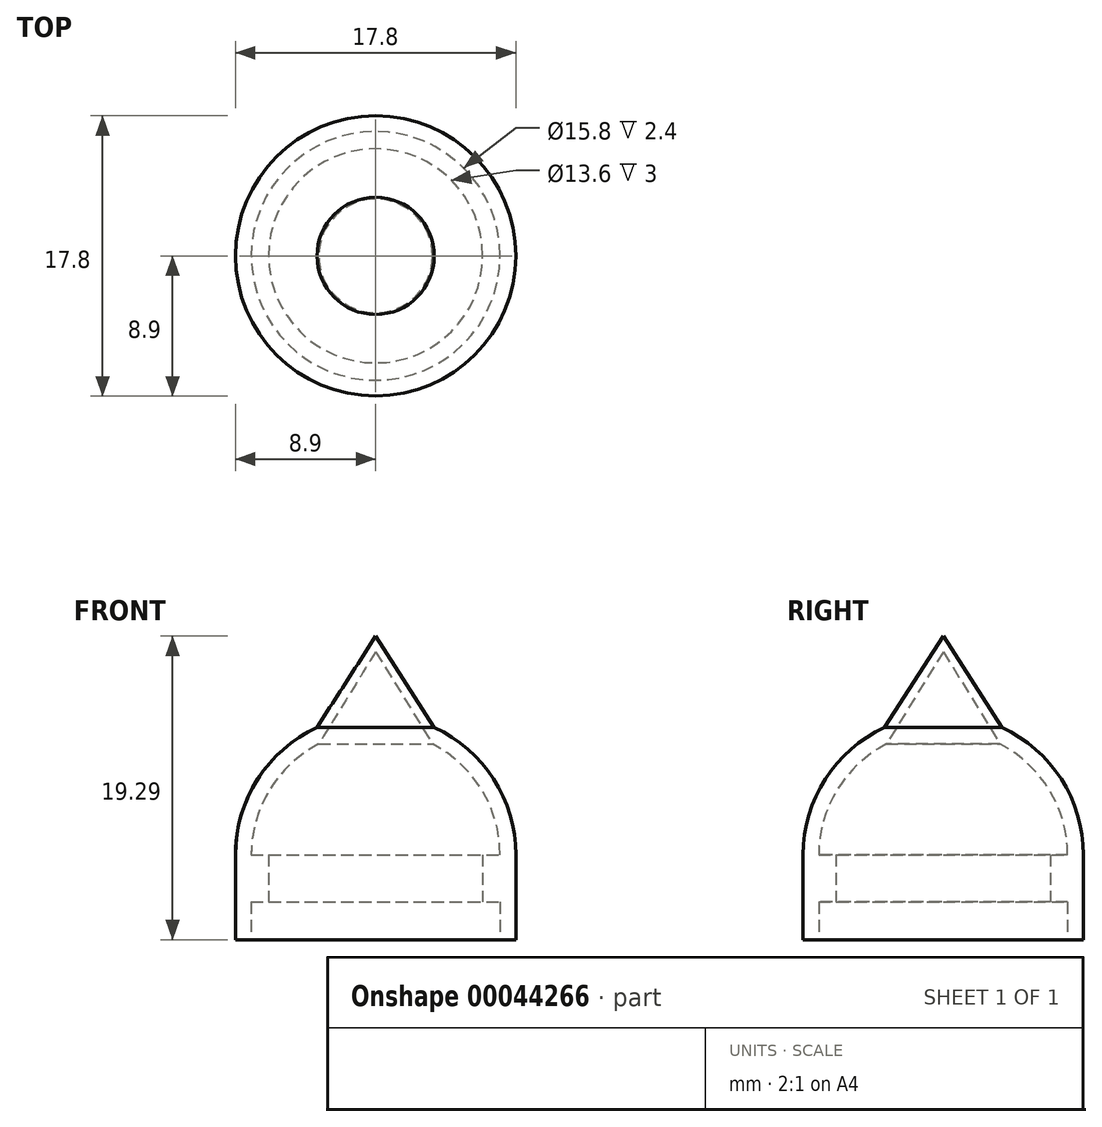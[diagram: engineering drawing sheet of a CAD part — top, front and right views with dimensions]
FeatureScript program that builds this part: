
annotation { "Feature Type Name" : "Feature", "Feature Type Description" : "" }
export const myFeature = defineFeature(function(context is Context, id is Id, definition is map)
    precondition{}
    {
        {
            var Q0;
            Q0=qCreatedBy(makeId("Top.planeOp"),FACE);
            var sketch = newSketch(context, id + "F0", { "sketchPlane" : qUnion([Q0])});
            skLineSegment(sketch, "E0", {"start": v(-17.52, 0) * mm, "end": v(42.68, 0) * mm, "construction": true});
            skLineSegment(sketch, "E1", {"start": v(0, 0) * mm, "end": v(0, 7.9) * mm, "construction": true});
            skLineSegment(sketch, "E2", {"start": v(0, 7.9) * mm, "end": v(2.4, 7.9) * mm});
            skLineSegment(sketch, "E3", {"start": v(2.4, 6.8) * mm, "end": v(2.4, 7.9) * mm});
            skLineSegment(sketch, "E4", {"start": v(2.4, 6.8) * mm, "end": v(5.4, 6.8) * mm});
            skLineSegment(sketch, "E5", {"start": v(0, 7.9) * mm, "end": v(0, 8.9) * mm});
            skLineSegment(sketch, "E6", {"start": v(5.4, 6.8) * mm, "end": v(5.4, 7.9) * mm});
            skLineSegment(sketch, "E7", {"start": v(0, 8.9) * mm, "end": v(5.4, 8.9) * mm});
            skArc(sketch, "E8", {"start": v(5.4, 8.9) * mm, "mid": v(10.2, 7.5) * mm, "end": v(13.48, 3.72) * mm});
            skLineSegment(sketch, "E9", {"start": v(2.4, 7.9) * mm, "end": v(5.4, 7.9) * mm, "construction": true});
            skArc(sketch, "E10", {"start": v(5.4, 7.9) * mm, "mid": v(9.52, 6.74) * mm, "end": v(12.43, 3.61) * mm});
            skLineSegment(sketch, "E11", {"start": v(5.4, 8.9) * mm, "end": v(19.3, 0) * mm, "construction": true});
            skLineSegment(sketch, "E12", {"start": v(13.48, 3.72) * mm, "end": v(19.3, 0) * mm});
            skLineSegment(sketch, "E13", {"start": v(19.3, 0) * mm, "end": v(18.3, 0) * mm});
            skLineSegment(sketch, "E14", {"start": v(18.3, 0) * mm, "end": v(12.43, 3.61) * mm});
            skSolve(sketch);
        }
        {
            var Q0;
            Q0=makeQuery(id+"F0.imprint","IMPRINT",FACE,{"disambiguationData":[TD([[makeQuery(id+"F0.imprint","IMPRINT",EDGE,{"derivedFrom":sQuery(id+"F0.wireOp",EDGE,"E2")}),1.0]])]});
            var Q1;
            Q1=sQuery(id+"F0.wireOp",EDGE,"E0");
            revolve(context, id + "F1", {"entities" : qUnion([Q0]), "axis" : qUnion([Q1]), "revolveType" : RevolveType.FULL});
        }
        {
            var Q0;
            Q0=qCreatedBy(makeId("Front.planeOp"),FACE);
            var sketch = newSketch(context, id + "F2", { "sketchPlane" : qUnion([Q0])});
            skCircle(sketch, "E15", {"center": v(0, 0) * mm, "radius": 7.26 * mm});
            skSolve(sketch);
        }
        {
            var Q0;
            Q0=makeQuery(id+"F1.opRevolve","SWEPT_BODY",BODY,{"disambiguationData":[OSD([sQuery(id+"F0.wireOp",EDGE,"E2"),sQuery(id+"F0.wireOp",EDGE,"E3"),sQuery(id+"F0.wireOp",EDGE,"E4"),sQuery(id+"F0.wireOp",EDGE,"E5"),sQuery(id+"F0.wireOp",EDGE,"E6"),sQuery(id+"F0.wireOp",EDGE,"E7"),sQuery(id+"F0.wireOp",EDGE,"E8"),sQuery(id+"F0.wireOp",EDGE,"E10"),sQuery(id+"F0.wireOp",EDGE,"E12"),sQuery(id+"F0.wireOp",EDGE,"E13"),sQuery(id+"F0.wireOp",EDGE,"E14")])]});
            var Q1;
            Q1=sQuery(id+"F2.wireOp",EDGE,"E15");
            transform(context, id + "F3", {"entities" : qUnion([Q0]), "transformType" : TransformType.ROTATION, "transformAxis" : qUnion([Q1]), "angle" : 90 * degree, "makeCopy" : false});
        }
    });
